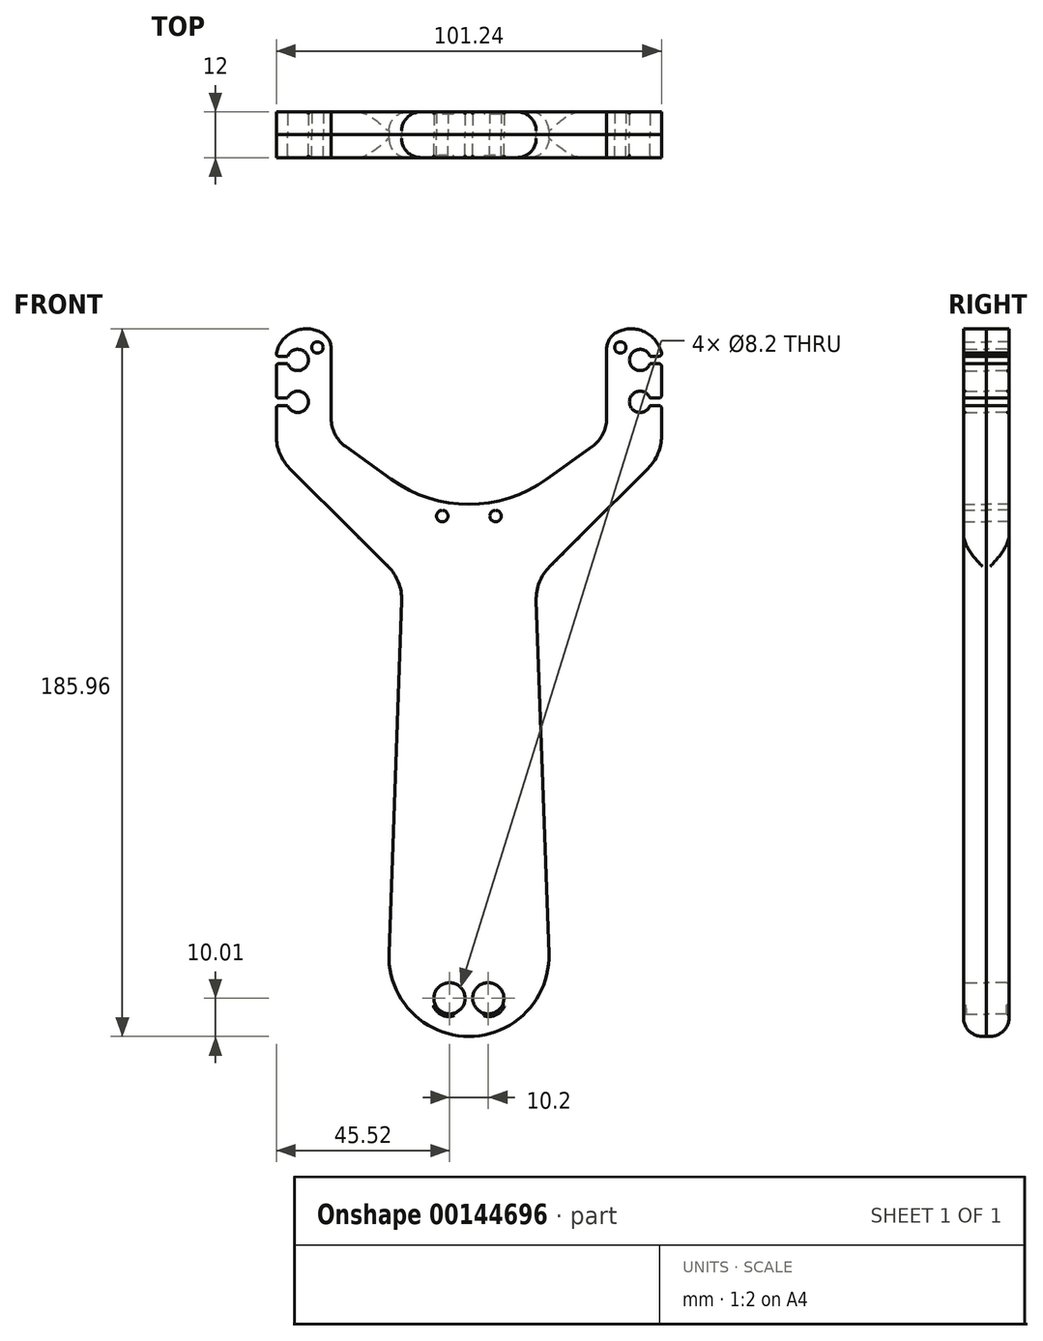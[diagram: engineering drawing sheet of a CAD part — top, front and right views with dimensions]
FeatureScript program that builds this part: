
annotation { "Feature Type Name" : "Feature", "Feature Type Description" : "" }
export const myFeature = defineFeature(function(context is Context, id is Id, definition is map)
    precondition{}
    {
        {
            var Q0;
            Q0=qCreatedBy(makeId("Front.planeOp"),FACE);
            var sketch = newSketch(context, id + "F0", { "sketchPlane" : qUnion([Q0])});
            skLineSegment(sketch, "E0", {"start": v(-36.2, 48.87) * mm, "end": v(-36.2, 30.62) * mm});
            skLineSegment(sketch, "E1", {"start": v(-32.45, 23.3) * mm, "end": v(-20.42, 14.66) * mm});
            skArc(sketch, "E2", {"start": v(-38.99, 53.35) * mm, "mid": v(-46.15, 53.4) * mm, "end": v(-50.62, 47.8) * mm});
            skArc(sketch, "E3", {"start": v(-47.62, 45) * mm, "mid": v(-42.2, 46) * mm, "end": v(-47.62, 47) * mm});
            skArc(sketch, "E4", {"start": v(-47.62, 34) * mm, "mid": v(-42.2, 35) * mm, "end": v(-47.62, 36) * mm});
            skLineSegment(sketch, "E5", {"start": v(-47.62, 47) * mm, "end": v(-50.62, 47) * mm});
            skLineSegment(sketch, "E6", {"start": v(-47.62, 45) * mm, "end": v(-50.62, 45) * mm});
            skLineSegment(sketch, "E7", {"start": v(-47.62, 36) * mm, "end": v(-50.62, 36) * mm});
            skLineSegment(sketch, "E8", {"start": v(-47.62, 34) * mm, "end": v(-50.62, 34) * mm});
            skLineSegment(sketch, "E9", {"start": v(-50.62, 47) * mm, "end": v(-50.62, 47.8) * mm});
            skLineSegment(sketch, "E10", {"start": v(-50.62, 45) * mm, "end": v(-50.62, 36) * mm});
            skLineSegment(sketch, "E11", {"start": v(-50.62, 34) * mm, "end": v(-50.62, 26) * mm});
            skLineSegment(sketch, "E12", {"start": v(-47.09, 17.5) * mm, "end": v(-21.2, -8.3) * mm});
            skPoint(sketch, "E13.visualSharp", {"position": v(-36.2, 26) * mm});
            skArc(sketch, "E13.filletArc", {"start": v(-36.2, 30.62) * mm, "mid": v(-35.2, 26.5) * mm, "end": v(-32.45, 23.3) * mm});
            skPoint(sketch, "E14.visualSharp", {"position": v(-50.62, 21.02) * mm});
            skArc(sketch, "E14.filletArc", {"start": v(-50.62, 26) * mm, "mid": v(-49.7, 21.4) * mm, "end": v(-47.09, 17.5) * mm});
            skPoint(sketch, "E15.visualSharp", {"position": v(-36.2, 51.1) * mm});
            skArc(sketch, "E15.filletArc", {"start": v(-36.2, 48.87) * mm, "mid": v(-36.95, 51.51) * mm, "end": v(-38.99, 53.35) * mm});
            skLineSegment(sketch, "E16.MirrorCS", {"start": v(47.62, 36) * mm, "end": v(50.62, 36) * mm});
            skArc(sketch, "E17.MirrorCS", {"start": v(38.99, 53.35) * mm, "mid": v(46.15, 53.4) * mm, "end": v(50.62, 47.8) * mm});
            skLineSegment(sketch, "E18.MirrorCS", {"start": v(47.62, 47) * mm, "end": v(50.62, 47) * mm});
            skLineSegment(sketch, "E19.MirrorCS", {"start": v(47.62, 45) * mm, "end": v(50.62, 45) * mm});
            skLineSegment(sketch, "E20.MirrorCS", {"start": v(50.62, 47) * mm, "end": v(50.62, 47.8) * mm});
            skLineSegment(sketch, "E21.MirrorCS", {"start": v(47.62, 34) * mm, "end": v(50.62, 34) * mm});
            skLineSegment(sketch, "E22.MirrorCS", {"start": v(50.62, 34) * mm, "end": v(50.62, 26) * mm});
            skArc(sketch, "E23.MirrorCS", {"start": v(36.2, 48.87) * mm, "mid": v(36.95, 51.51) * mm, "end": v(38.99, 53.35) * mm});
            skLineSegment(sketch, "E24.MirrorCS", {"start": v(36.2, 48.87) * mm, "end": v(36.2, 30.62) * mm});
            skPoint(sketch, "E25.MirrorP", {"position": v(50.62, 21.02) * mm});
            skPoint(sketch, "E26.MirrorP", {"position": v(36.2, 51.1) * mm});
            skArc(sketch, "E27.MirrorCS", {"start": v(50.62, 26) * mm, "mid": v(49.7, 21.4) * mm, "end": v(47.09, 17.5) * mm});
            skArc(sketch, "E28.MirrorCS", {"start": v(47.62, 45) * mm, "mid": v(42.2, 46) * mm, "end": v(47.62, 47) * mm});
            skArc(sketch, "E29.MirrorCS", {"start": v(47.62, 34) * mm, "mid": v(42.2, 35) * mm, "end": v(47.62, 36) * mm});
            skArc(sketch, "E30.MirrorCS", {"start": v(36.2, 30.62) * mm, "mid": v(35.2, 26.5) * mm, "end": v(32.45, 23.3) * mm});
            skLineSegment(sketch, "E31.MirrorCS", {"start": v(47.09, 17.5) * mm, "end": v(21.2, -8.3) * mm});
            skLineSegment(sketch, "E32.MirrorCS", {"start": v(32.45, 23.3) * mm, "end": v(20.42, 14.66) * mm});
            skLineSegment(sketch, "E33.MirrorCS", {"start": v(50.62, 45) * mm, "end": v(50.62, 36) * mm});
            skPoint(sketch, "E34.MirrorP", {"position": v(36.2, 26) * mm});
            skPoint(sketch, "E35.visualSharp", {"position": v(0, 0) * mm});
            skArc(sketch, "E35.filletArc", {"start": v(-20.42, 14.66) * mm, "mid": v(0, 8.1) * mm, "end": v(20.42, 14.66) * mm});
            skLineSegment(sketch, "E36", {"start": v(-17.69, -17.23) * mm, "end": v(-21, -110) * mm});
            skLineSegment(sketch, "E37.MirrorCS", {"start": v(17.69, -17.23) * mm, "end": v(21, -110) * mm});
            skArc(sketch, "E38", {"start": v(-21, -110) * mm, "mid": v(0, -131.76) * mm, "end": v(21, -110) * mm});
            skPoint(sketch, "E39.visualSharp", {"position": v(-17.5, -12) * mm});
            skArc(sketch, "E39.filletArc", {"start": v(-17.69, -17.23) * mm, "mid": v(-18.52, -12.4) * mm, "end": v(-21.2, -8.3) * mm});
            skPoint(sketch, "E40.visualSharp", {"position": v(17.5, -12) * mm});
            skArc(sketch, "E40.filletArc", {"start": v(21.2, -8.3) * mm, "mid": v(18.52, -12.4) * mm, "end": v(17.69, -17.23) * mm});
            skCircle(sketch, "E41", {"center": v(-39.8, 49.3) * mm, "radius": 1.5 * mm});
            skCircle(sketch, "E42.MirrorC", {"center": v(39.8, 49.3) * mm, "radius": 1.5 * mm});
            skCircle(sketch, "E43", {"center": v(-7, 5) * mm, "radius": 1.5 * mm});
            skCircle(sketch, "E44", {"center": v(7, 5) * mm, "radius": 1.5 * mm});
            skLineSegment(sketch, "E45", {"start": v(-7, 5) * mm, "end": v(7, 5) * mm, "construction": true});
            skPoint(sketch, "E46", {"position": v(0, 5) * mm});
            skCircle(sketch, "E47", {"center": v(-5.1, -121.75) * mm, "radius": 4.1 * mm});
            skCircle(sketch, "E48", {"center": v(5.1, -121.75) * mm, "radius": 4.1 * mm});
            skLineSegment(sketch, "E49", {"start": v(-5.1, -121.75) * mm, "end": v(5.1, -121.75) * mm, "construction": true});
            skPoint(sketch, "E50", {"position": v(0, -121.75) * mm});
            skSolve(sketch);
        }
        {
            var Q0;
            Q0 = qSketchRegion(id + "F0", true);
            extrude(context, id + "F1", {"entities" : qUnion([Q0]), "depth" : 6 * mm});
        }
        {
            var Q0;
            Q0=makeQuery(id+"F1.opExtrude","CAP_EDGE",EDGE,{"disambiguationData":[OSD([sQuery(id+"F0.wireOp",EDGE,"E39.filletArc")])],"isStart":false});
            var Q1;
            Q1=makeQuery(id+"F1.opExtrude","CAP_EDGE",EDGE,{"disambiguationData":[OSD([sQuery(id+"F0.wireOp",EDGE,"E36")])],"isStart":false});
            var Q2;
            Q2=makeQuery(id+"F1.opExtrude","CAP_EDGE",EDGE,{"disambiguationData":[OSD([sQuery(id+"F0.wireOp",EDGE,"E38")])],"isStart":false});
            var Q3;
            Q3=makeQuery(id+"F1.opExtrude","CAP_EDGE",EDGE,{"disambiguationData":[OSD([sQuery(id+"F0.wireOp",EDGE,"E37.MirrorCS")])],"isStart":false});
            var Q4;
            Q4=makeQuery(id+"F1.opExtrude","CAP_EDGE",EDGE,{"disambiguationData":[OSD([sQuery(id+"F0.wireOp",EDGE,"E40.filletArc")])],"isStart":false});
            fillet(context, id + "F2", {"entities" : qUnion([Q0, Q1, Q2, Q3, Q4]), "radius" : 5 * mm, "allowEdgeOverflow" : false});
        }
        {
            var Q0;
            Q0=makeQuery(id+"F1.opExtrude","SWEPT_BODY",BODY,{"disambiguationData":[OSD([sQuery(id+"F0.wireOp",EDGE,"E0"),sQuery(id+"F0.wireOp",EDGE,"E1"),sQuery(id+"F0.wireOp",EDGE,"E2"),sQuery(id+"F0.wireOp",EDGE,"E3"),sQuery(id+"F0.wireOp",EDGE,"E4"),sQuery(id+"F0.wireOp",EDGE,"E5"),sQuery(id+"F0.wireOp",EDGE,"E6"),sQuery(id+"F0.wireOp",EDGE,"E7"),sQuery(id+"F0.wireOp",EDGE,"E8"),sQuery(id+"F0.wireOp",EDGE,"E9"),sQuery(id+"F0.wireOp",EDGE,"E10"),sQuery(id+"F0.wireOp",EDGE,"E11"),sQuery(id+"F0.wireOp",EDGE,"E12"),sQuery(id+"F0.wireOp",EDGE,"E13.filletArc"),sQuery(id+"F0.wireOp",EDGE,"E14.filletArc"),sQuery(id+"F0.wireOp",EDGE,"E15.filletArc"),sQuery(id+"F0.wireOp",EDGE,"E16.MirrorCS"),sQuery(id+"F0.wireOp",EDGE,"E17.MirrorCS"),sQuery(id+"F0.wireOp",EDGE,"E18.MirrorCS"),sQuery(id+"F0.wireOp",EDGE,"E19.MirrorCS"),sQuery(id+"F0.wireOp",EDGE,"E20.MirrorCS"),sQuery(id+"F0.wireOp",EDGE,"E21.MirrorCS"),sQuery(id+"F0.wireOp",EDGE,"E22.MirrorCS"),sQuery(id+"F0.wireOp",EDGE,"E23.MirrorCS"),sQuery(id+"F0.wireOp",EDGE,"E24.MirrorCS"),sQuery(id+"F0.wireOp",EDGE,"E27.MirrorCS"),sQuery(id+"F0.wireOp",EDGE,"E28.MirrorCS"),sQuery(id+"F0.wireOp",EDGE,"E29.MirrorCS"),sQuery(id+"F0.wireOp",EDGE,"E30.MirrorCS"),sQuery(id+"F0.wireOp",EDGE,"E31.MirrorCS"),sQuery(id+"F0.wireOp",EDGE,"E32.MirrorCS"),sQuery(id+"F0.wireOp",EDGE,"E33.MirrorCS"),sQuery(id+"F0.wireOp",EDGE,"E35.filletArc"),sQuery(id+"F0.wireOp",EDGE,"E36"),sQuery(id+"F0.wireOp",EDGE,"E37.MirrorCS"),sQuery(id+"F0.wireOp",EDGE,"E38"),sQuery(id+"F0.wireOp",EDGE,"E39.filletArc"),sQuery(id+"F0.wireOp",EDGE,"E40.filletArc"),sQuery(id+"F0.wireOp",EDGE,"E41"),sQuery(id+"F0.wireOp",EDGE,"E42.MirrorC"),sQuery(id+"F0.wireOp",EDGE,"E43"),sQuery(id+"F0.wireOp",EDGE,"E44"),sQuery(id+"F0.wireOp",EDGE,"E47"),sQuery(id+"F0.wireOp",EDGE,"E48")])]});
            var Q1;
            Q1=qCreatedBy(makeId("Front.planeOp"),FACE);
            mirror(context, id + "F3", {"entities" : qUnion([Q0]), "mirrorPlane" : qUnion([Q1])});
        }
        {
            var Q0;
            Q0=makeQuery(id+"F3.opPattern","COPY",EDGE,{"derivedFrom":makeQuery(id+"F1.opExtrude","CAP_EDGE",EDGE,{"disambiguationData":[OSD([sQuery(id+"F0.wireOp",EDGE,"E28.MirrorCS")])],"isStart":false}),"instanceName":"1"});
            var Q1;
            Q1=makeQuery(id+"F3.opPattern","COPY",EDGE,{"derivedFrom":makeQuery(id+"F1.opExtrude","CAP_EDGE",EDGE,{"disambiguationData":[OSD([sQuery(id+"F0.wireOp",EDGE,"E29.MirrorCS")])],"isStart":false}),"instanceName":"1"});
            var Q2;
            Q2=makeQuery(id+"F3.opPattern","COPY",EDGE,{"derivedFrom":makeQuery(id+"F1.opExtrude","CAP_EDGE",EDGE,{"disambiguationData":[OSD([sQuery(id+"F0.wireOp",EDGE,"E3")])],"isStart":false}),"instanceName":"1"});
            var Q3;
            Q3=makeQuery(id+"F3.opPattern","COPY",EDGE,{"derivedFrom":makeQuery(id+"F1.opExtrude","CAP_EDGE",EDGE,{"disambiguationData":[OSD([sQuery(id+"F0.wireOp",EDGE,"E4")])],"isStart":false}),"instanceName":"1"});
            var Q4;
            Q4=makeQuery(id+"F1.opExtrude","CAP_EDGE",EDGE,{"disambiguationData":[OSD([sQuery(id+"F0.wireOp",EDGE,"E28.MirrorCS")])],"isStart":false});
            var Q5;
            Q5=makeQuery(id+"F1.opExtrude","CAP_EDGE",EDGE,{"disambiguationData":[OSD([sQuery(id+"F0.wireOp",EDGE,"E29.MirrorCS")])],"isStart":false});
            var Q6;
            Q6=makeQuery(id+"F1.opExtrude","CAP_EDGE",EDGE,{"disambiguationData":[OSD([sQuery(id+"F0.wireOp",EDGE,"E3")])],"isStart":false});
            var Q7;
            Q7=makeQuery(id+"F1.opExtrude","CAP_EDGE",EDGE,{"disambiguationData":[OSD([sQuery(id+"F0.wireOp",EDGE,"E4")])],"isStart":false});
            var Q8;
            Q8=makeQuery(id+"F1.opExtrude","SWEPT_EDGE",EDGE,{"disambiguationData":[OSD([sQuery(id+"F0.wireOp",EDGE,"E5"),sQuery(id+"F0.wireOp",EDGE,"E9")])]});
            var Q9;
            Q9=makeQuery(id+"F3.opPattern","COPY",EDGE,{"derivedFrom":makeQuery(id+"F1.opExtrude","SWEPT_EDGE",EDGE,{"disambiguationData":[OSD([sQuery(id+"F0.wireOp",EDGE,"E5"),sQuery(id+"F0.wireOp",EDGE,"E9")])]}),"instanceName":"1"});
            var Q10;
            Q10=makeQuery(id+"F3.opPattern","COPY",EDGE,{"derivedFrom":makeQuery(id+"F1.opExtrude","SWEPT_EDGE",EDGE,{"disambiguationData":[OSD([sQuery(id+"F0.wireOp",EDGE,"E6"),sQuery(id+"F0.wireOp",EDGE,"E10")])]}),"instanceName":"1"});
            var Q11;
            Q11=makeQuery(id+"F1.opExtrude","SWEPT_EDGE",EDGE,{"disambiguationData":[OSD([sQuery(id+"F0.wireOp",EDGE,"E6"),sQuery(id+"F0.wireOp",EDGE,"E10")])]});
            var Q12;
            Q12=makeQuery(id+"F1.opExtrude","SWEPT_EDGE",EDGE,{"disambiguationData":[OSD([sQuery(id+"F0.wireOp",EDGE,"E7"),sQuery(id+"F0.wireOp",EDGE,"E10")])]});
            var Q13;
            Q13=makeQuery(id+"F1.opExtrude","SWEPT_EDGE",EDGE,{"disambiguationData":[OSD([sQuery(id+"F0.wireOp",EDGE,"E8"),sQuery(id+"F0.wireOp",EDGE,"E11")])]});
            var Q14;
            Q14=makeQuery(id+"F3.opPattern","COPY",EDGE,{"derivedFrom":makeQuery(id+"F1.opExtrude","SWEPT_EDGE",EDGE,{"disambiguationData":[OSD([sQuery(id+"F0.wireOp",EDGE,"E7"),sQuery(id+"F0.wireOp",EDGE,"E10")])]}),"instanceName":"1"});
            var Q15;
            Q15=makeQuery(id+"F3.opPattern","COPY",EDGE,{"derivedFrom":makeQuery(id+"F1.opExtrude","SWEPT_EDGE",EDGE,{"disambiguationData":[OSD([sQuery(id+"F0.wireOp",EDGE,"E8"),sQuery(id+"F0.wireOp",EDGE,"E11")])]}),"instanceName":"1"});
            var Q16;
            Q16=makeQuery(id+"F1.opExtrude","SWEPT_EDGE",EDGE,{"disambiguationData":[OSD([sQuery(id+"F0.wireOp",EDGE,"E18.MirrorCS"),sQuery(id+"F0.wireOp",EDGE,"E20.MirrorCS")])]});
            var Q17;
            Q17=makeQuery(id+"F1.opExtrude","SWEPT_EDGE",EDGE,{"disambiguationData":[OSD([sQuery(id+"F0.wireOp",EDGE,"E19.MirrorCS"),sQuery(id+"F0.wireOp",EDGE,"E33.MirrorCS")])]});
            var Q18;
            Q18=makeQuery(id+"F1.opExtrude","SWEPT_EDGE",EDGE,{"disambiguationData":[OSD([sQuery(id+"F0.wireOp",EDGE,"E16.MirrorCS"),sQuery(id+"F0.wireOp",EDGE,"E33.MirrorCS")])]});
            var Q19;
            Q19=makeQuery(id+"F1.opExtrude","SWEPT_EDGE",EDGE,{"disambiguationData":[OSD([sQuery(id+"F0.wireOp",EDGE,"E21.MirrorCS"),sQuery(id+"F0.wireOp",EDGE,"E22.MirrorCS")])]});
            var Q20;
            Q20=makeQuery(id+"F3.opPattern","COPY",EDGE,{"derivedFrom":makeQuery(id+"F1.opExtrude","SWEPT_EDGE",EDGE,{"disambiguationData":[OSD([sQuery(id+"F0.wireOp",EDGE,"E18.MirrorCS"),sQuery(id+"F0.wireOp",EDGE,"E20.MirrorCS")])]}),"instanceName":"1"});
            var Q21;
            Q21=makeQuery(id+"F3.opPattern","COPY",EDGE,{"derivedFrom":makeQuery(id+"F1.opExtrude","SWEPT_EDGE",EDGE,{"disambiguationData":[OSD([sQuery(id+"F0.wireOp",EDGE,"E19.MirrorCS"),sQuery(id+"F0.wireOp",EDGE,"E33.MirrorCS")])]}),"instanceName":"1"});
            var Q22;
            Q22=makeQuery(id+"F3.opPattern","COPY",EDGE,{"derivedFrom":makeQuery(id+"F1.opExtrude","SWEPT_EDGE",EDGE,{"disambiguationData":[OSD([sQuery(id+"F0.wireOp",EDGE,"E16.MirrorCS"),sQuery(id+"F0.wireOp",EDGE,"E33.MirrorCS")])]}),"instanceName":"1"});
            var Q23;
            Q23=makeQuery(id+"F3.opPattern","COPY",EDGE,{"derivedFrom":makeQuery(id+"F1.opExtrude","SWEPT_EDGE",EDGE,{"disambiguationData":[OSD([sQuery(id+"F0.wireOp",EDGE,"E21.MirrorCS"),sQuery(id+"F0.wireOp",EDGE,"E22.MirrorCS")])]}),"instanceName":"1"});
            var Q24;
            Q24=makeQuery(id+"F1.opExtrude","CAP_EDGE",EDGE,{"disambiguationData":[OSD([sQuery(id+"F0.wireOp",EDGE,"E47")])],"isStart":false});
            var Q25;
            Q25=makeQuery(id+"F1.opExtrude","CAP_EDGE",EDGE,{"disambiguationData":[OSD([sQuery(id+"F0.wireOp",EDGE,"E48")])],"isStart":false});
            var Q26;
            Q26=makeQuery(id+"F3.opPattern","COPY",EDGE,{"derivedFrom":makeQuery(id+"F1.opExtrude","CAP_EDGE",EDGE,{"disambiguationData":[OSD([sQuery(id+"F0.wireOp",EDGE,"E48")])],"isStart":false}),"instanceName":"1"});
            var Q27;
            Q27=makeQuery(id+"F3.opPattern","COPY",EDGE,{"derivedFrom":makeQuery(id+"F1.opExtrude","CAP_EDGE",EDGE,{"disambiguationData":[OSD([sQuery(id+"F0.wireOp",EDGE,"E47")])],"isStart":false}),"instanceName":"1"});
            fillet(context, id + "F4", {"entities" : qUnion([Q0, Q1, Q2, Q3, Q4, Q5, Q6, Q7, Q8, Q9, Q10, Q11, Q12, Q13, Q14, Q15, Q16, Q17, Q18, Q19, Q20, Q21, Q22, Q23, Q24, Q25, Q26, Q27]), "radius" : 0.6 * mm, "tangentPropagation" : true, "allowEdgeOverflow" : false});
        }
    });
